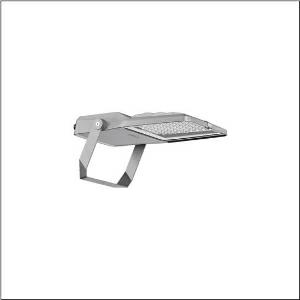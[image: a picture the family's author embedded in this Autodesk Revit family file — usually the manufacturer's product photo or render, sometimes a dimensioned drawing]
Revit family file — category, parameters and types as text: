
# Revit family: floodlight_fl_21_iq_mini___rs12_5xa7771c4b1a_004d
name_source: partatom
category: Lighting Fixtures
units: mm (PartAtom-declared; Revit-internal decimal feet)

## family parameters
Cut with Voids When Loaded = No
Host = Face
Light Source = No
Part Type = Normal
Room Calculation Point = No
Round Connector Dimension = Use Diameter
Shared = No

## types (1)
- --- (1 x LED, 12860 lm, 87.2 W, 4000K)
    Apparent Load = 87 VA
    CIE Flux Codes = 79 92 99 100 100
    Color Rendering = 70
    Color Temperature = 4000K
    Default Elevation = 1800 mm
    Description = Floodlight FL 21 iQ mini, floodlight, primary light control with lens, of PMMA, primary optical cover: protective disc, of toughened safety glass, transparent, light distribution: RS12, light emission: direct distribution, installation type: surface-mounted, lamps: LED, High Power LED, rated values: 12.860lm | 87,2W | 147,5lm/W (begin service life); end service life: 12.860lm | 92,1W; at 50% lumin. flux: 6.430lm | 40,2W | 160lm/W, colour temperature: 4000K, colour rendering: CRI > 70, light colour: 740, light setting 1 begin service life: 100% | 12.860lm | 87,2W | 147,5lm/W | 4.000K, light setting 1 end service life: 92,1W, further light settings possible, control: Auto-Match, Temp-Guard, Lumen-Switch, Night-Set, Smart-Wire, Light-Fading, Desk-Remote (wireless, voltage-free reading and setting of iQ features in the workshop via application-optimized NFC function/RFID function), optimised constant luminous flux control (CLO 2.0), pre-setting: linear dimming characteristic, with terminal, 6-pole, mains connection: 220..240V, AC, 50/60Hz, luminaire housing, of diecast aluminium, powder-coated, SITECO metallic grey (DB 702S), corrosivity category C5 mid according to DIN EN ISO 12944suitable for swimming poolschlorine-resistant, sealing non-destructively replaceable, mounting bracket, of steel, galvanised, powder-coated, SITECO metallic grey (DB 702S), protection rating (complete): IP66, insulation class (complete): insulation class II (safety insulation), certification: CE, ENEC, VDE, protection symbol: D, impact resistance: IK08, permissible operating ambient temperature: -40..+40°C, permissible operating ambient temperature for outdoor applications: -40..+50°C, standard: DIN EN 12944, LABS conformity tested according to VDMA 24364:2018-05, packaging unit: 1 piece

Light Distribution: RS12
    Height = 70 mm
    Lamp = 1 x LED
    Lamp Light Flux = 12860 lm
    Lamp Power = 87.2 W
    Lamp count = 1
    Length = 485 mm
    Luminous efficacy = 147 lm/W
    Manufacturer = Siteco
    ModVariant = No
    Model = 5XA7771C4B1A
    Number of Poles = 1
    OnlyDefault = Yes
    Power Factor = 1
    Product Name = Floodlight FL 21 iQ mini | RS12
    Product group = floodlight | pylon annexe
    ProductGroupID = 6201
    Protection Class = Protection class II
    Protection Degree = IP 66
    RLX_Detail_Level = 1
    RLX_Emergency_Light_Flux = 0 lm
    RLX_Emergency_Type = 0
    RLX_Emergency_Type_DB = No
    RlxData = <blob elided: 91237 chars, md5=6b6f8f7d>
    Socket = socket
    Standby Power = 0 W
    System Light Flux = 12860 lm
    System Power = 87 W
    Type Comments = factory setting: luminous flux: 100 % | dim-lin: 254 | 456 mA
    Type Image = l_1006845.jpg
    URL = http://relux.com
    VarID = @adj_167185
    Voltage = 0 V
    Weight = 0.00 kg
    Width = 337 mm

## geometry (parser evidence)
native form markers: Blend x4, Sweep x13
no freeform markers — native parametric forms only
